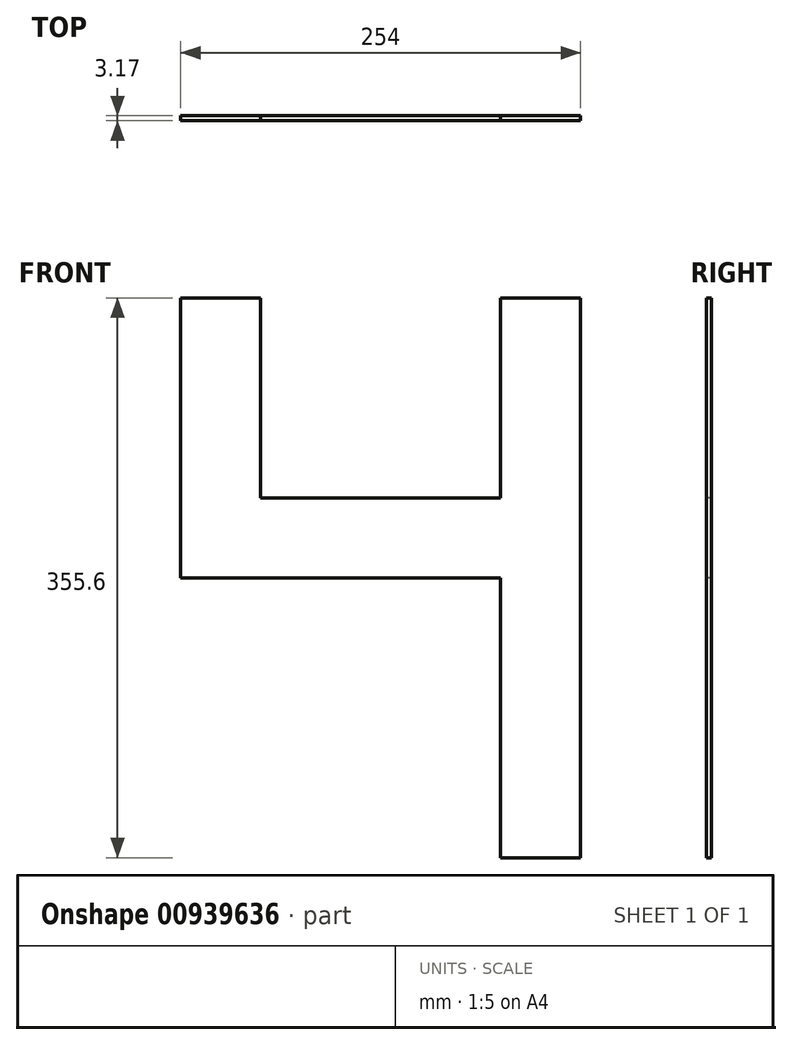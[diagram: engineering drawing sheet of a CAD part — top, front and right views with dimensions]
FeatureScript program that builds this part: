
annotation { "Feature Type Name" : "Feature", "Feature Type Description" : "" }
export const myFeature = defineFeature(function(context is Context, id is Id, definition is map)
    precondition{}
    {
        {
            var Q0;
            Q0=qCreatedBy(makeId("Front.planeOp"),FACE);
            var sketch = newSketch(context, id + "F0", { "sketchPlane" : qUnion([Q0])});
            skLineSegment(sketch, "E0.bottom", {"start": v(0, 0) * mm, "end": v(-50.8, 0) * mm});
            skLineSegment(sketch, "E0.top", {"start": v(0, 355.6) * mm, "end": v(-50.8, 355.6) * mm});
            skLineSegment(sketch, "E0.left", {"start": v(0, 0) * mm, "end": v(0, 355.6) * mm});
            skLineSegment(sketch, "E0.right", {"start": v(-50.8, 0) * mm, "end": v(-50.8, 355.6) * mm});
            skLineSegment(sketch, "E1.bottom", {"start": v(-50.8, 177.8) * mm, "end": v(-254, 177.8) * mm});
            skLineSegment(sketch, "E1.top", {"start": v(-50.8, 228.6) * mm, "end": v(-254, 228.6) * mm});
            skLineSegment(sketch, "E1.left", {"start": v(-50.8, 177.8) * mm, "end": v(-50.8, 228.6) * mm});
            skLineSegment(sketch, "E1.right", {"start": v(-254, 177.8) * mm, "end": v(-254, 228.6) * mm});
            skLineSegment(sketch, "E2.bottom", {"start": v(-254, 228.6) * mm, "end": v(-203.2, 228.6) * mm});
            skLineSegment(sketch, "E2.top", {"start": v(-254, 355.6) * mm, "end": v(-203.2, 355.6) * mm});
            skLineSegment(sketch, "E2.left", {"start": v(-254, 228.6) * mm, "end": v(-254, 355.6) * mm});
            skLineSegment(sketch, "E2.right", {"start": v(-203.2, 228.6) * mm, "end": v(-203.2, 355.6) * mm});
            skSolve(sketch);
        }
        {
            var Q0;
            Q0 = qSketchRegion(id + "F0", true);
            extrude(context, id + "F1", {"entities" : qUnion([Q0]), "oppositeDirection" : true, "depth" : 3.17 * mm, "offsetDistance" : 25.4 * mm});
        }
    });
